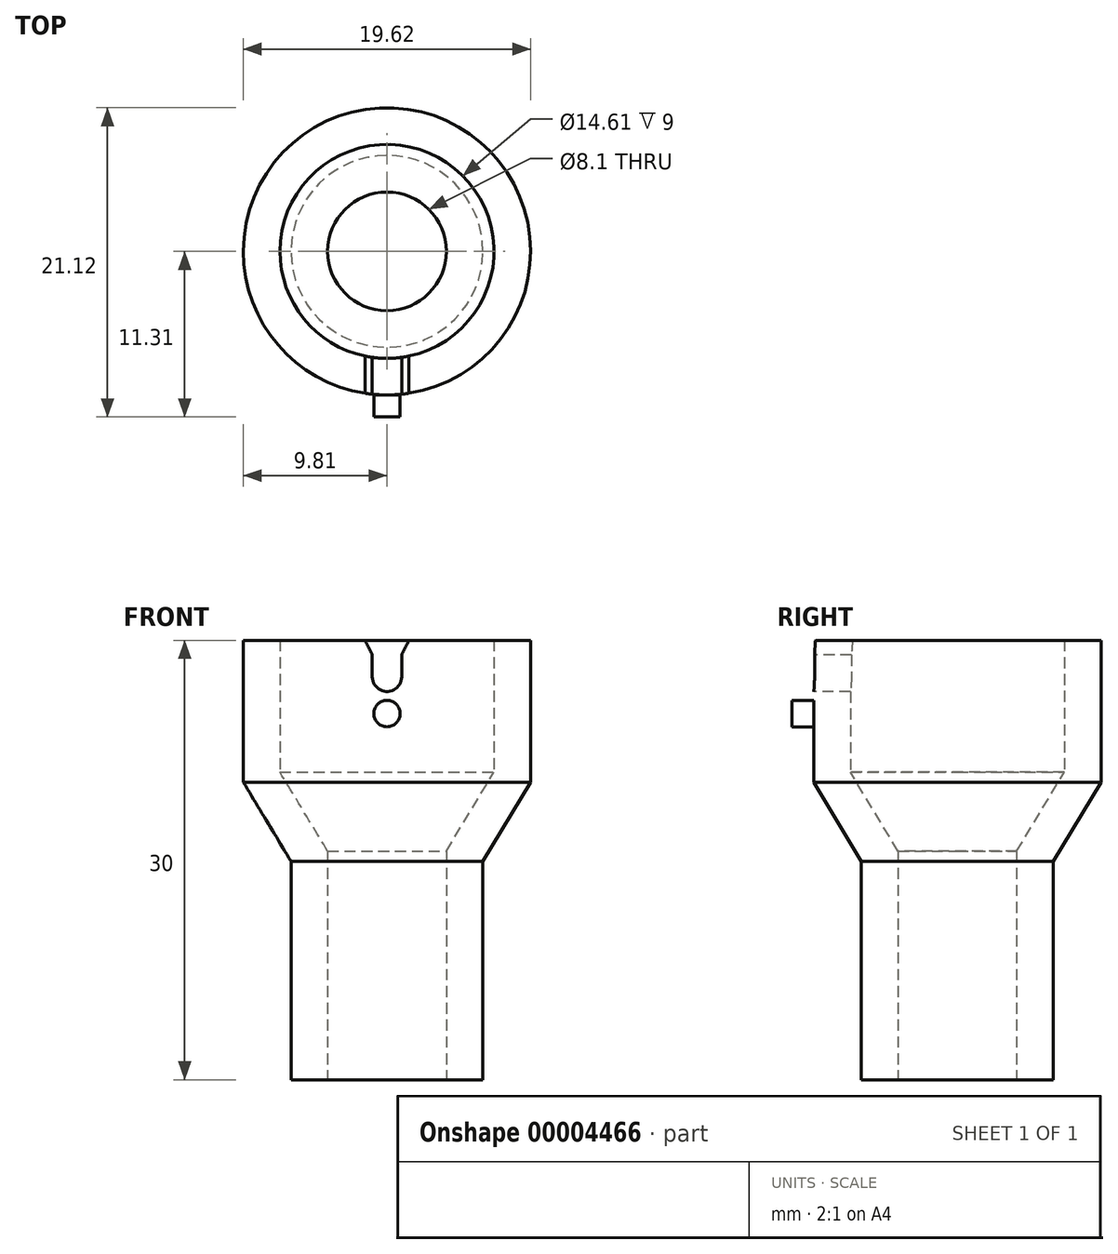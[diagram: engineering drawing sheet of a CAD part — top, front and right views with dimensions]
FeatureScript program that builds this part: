
annotation { "Feature Type Name" : "Feature", "Feature Type Description" : "" }
export const myFeature = defineFeature(function(context is Context, id is Id, definition is map)
    precondition{}
    {
        {
            var Q0;
            Q0=qCreatedBy(makeId("Front.planeOp"),FACE);
            var sketch = newSketch(context, id + "F0", { "sketchPlane" : qUnion([Q0])});
            skLineSegment(sketch, "E0", {"start": v(4.05, 0) * mm, "end": v(4.05, 15.6) * mm});
            skLineSegment(sketch, "E1", {"start": v(4.05, 15.6) * mm, "end": v(7.3, 21) * mm});
            skLineSegment(sketch, "E2", {"start": v(7.3, 21) * mm, "end": v(7.3, 30) * mm});
            skLineSegment(sketch, "E3.0", {"start": v(9.8, 20.3) * mm, "end": v(9.8, 30) * mm});
            skLineSegment(sketch, "E3.1", {"start": v(6.55, 14.9) * mm, "end": v(9.8, 20.3) * mm});
            skLineSegment(sketch, "E3.2", {"start": v(6.55, 0) * mm, "end": v(6.55, 14.9) * mm});
            skLineSegment(sketch, "E4", {"start": v(7.3, 30) * mm, "end": v(9.8, 30) * mm});
            skLineSegment(sketch, "E5", {"start": v(4.05, 0) * mm, "end": v(6.55, 0) * mm});
            skLineSegment(sketch, "E6", {"start": v(0, 0) * mm, "end": v(0, 16.66) * mm, "construction": true});
            skSolve(sketch);
        }
        {
            var Q0;
            Q0=makeQuery(id+"F0.imprint","IMPRINT",FACE,{"disambiguationData":[TD([[makeQuery(id+"F0.imprint","IMPRINT",EDGE,{"derivedFrom":sQuery(id+"F0.wireOp",EDGE,"E0")}),-1.0]])]});
            var Q1;
            Q1=sQuery(id+"F0.wireOp",EDGE,"E6");
            revolve(context, id + "F1", {"entities" : qUnion([Q0]), "axis" : qUnion([Q1]), "revolveType" : RevolveType.FULL});
        }
        {
            var Q0;
            Q0=makeQuery(id+"F1.opRevolve","SWEPT_FACE",FACE,{"disambiguationData":[OSD([sQuery(id+"F0.wireOp",EDGE,"E4")])]});
            var sketch = newSketch(context, id + "F2", { "sketchPlane" : qUnion([Q0])});
            skLineSegment(sketch, "E7", {"start": v(-7.98, -9.8) * mm, "end": v(7.98, -9.8) * mm, "construction": true});
            skPoint(sketch, "E8", {"position": v(0, -9.8) * mm});
            skSolve(sketch);
        }
        {
            var Q0;
            Q0=sQuery(id+"F2.wireOp",EDGE,"E7");
            cPlane(context, id + "F3", {"entities" : qUnion([Q0]), "cplaneType" : CPlaneType.LINE_ANGLE, "offset" : 150 * mm, "angle" : 0 * degree, "width" : 150 * mm, "height" : 150 * mm});
        }
        {
            var Q0;
            Q0=qCreatedBy(id+"F3.planeOp",FACE);
            var sketch = newSketch(context, id + "F4", { "sketchPlane" : qUnion([Q0])});
            skLineSegment(sketch, "E9", {"start": v(-1, 29) * mm, "end": v(-1, 27.5) * mm});
            skArc(sketch, "E10", {"start": v(-1, 27.5) * mm, "mid": v(-0.7, 26.8) * mm, "end": v(0, 26.5) * mm});
            skLineSegment(sketch, "E11", {"start": v(0, 0) * mm, "end": v(0, 30) * mm, "construction": true});
            skCircle(sketch, "E12", {"center": v(0, 25) * mm, "radius": 0.9 * mm});
            skLineSegment(sketch, "E13", {"start": v(-1, 29) * mm, "end": v(-1.5, 30) * mm});
            skLineSegment(sketch, "E14", {"start": v(-1.5, 30) * mm, "end": v(0, 30) * mm});
            skLineSegment(sketch, "E15.0.MirrorCS", {"start": v(1.5, 30) * mm, "end": v(0, 30) * mm});
            skLineSegment(sketch, "E16.0.MirrorCS", {"start": v(1, 29) * mm, "end": v(1.5, 30) * mm});
            skLineSegment(sketch, "E17.0.MirrorCS", {"start": v(1, 29) * mm, "end": v(1, 27.5) * mm});
            skArc(sketch, "E18.0.MirrorCS", {"start": v(1, 27.5) * mm, "mid": v(0.7, 26.8) * mm, "end": v(0, 26.5) * mm});
            skSolve(sketch);
        }
        {
            var Q0;
            Q0=makeQuery(id+"F4.imprint","IMPRINT",FACE,{"disambiguationData":[TD([[makeQuery(id+"F4.imprint","IMPRINT",EDGE,{"derivedFrom":sQuery(id+"F4.wireOp",EDGE,"E12")}),1.0]])]});
            extrude(context, id + "F5", {"entities" : qUnion([Q0]), "oppositeDirection" : true, "depth" : 1.5 * mm});
        }
        {
            var Q0;
            Q0=makeQuery(id+"F4.imprint","IMPRINT",FACE,{"disambiguationData":[TD([[makeQuery(id+"F4.imprint","IMPRINT",EDGE,{"derivedFrom":sQuery(id+"F4.wireOp",EDGE,"E9")}),1.0]])]});
            var Q1;
            Q1=makeQuery(id+"F1.opRevolve","SWEPT_FACE",FACE,{"disambiguationData":[OSD([sQuery(id+"F0.wireOp",EDGE,"E2")])]});
            extrude(context, id + "F6", {"entities" : qUnion([Q0]), "operationType" : NewBodyOperationType.REMOVE, "endBound" : BoundingType.UP_TO_SURFACE, "endBoundEntityFace" : qUnion([Q1]), "depth" : 25 * mm});
        }
    });
